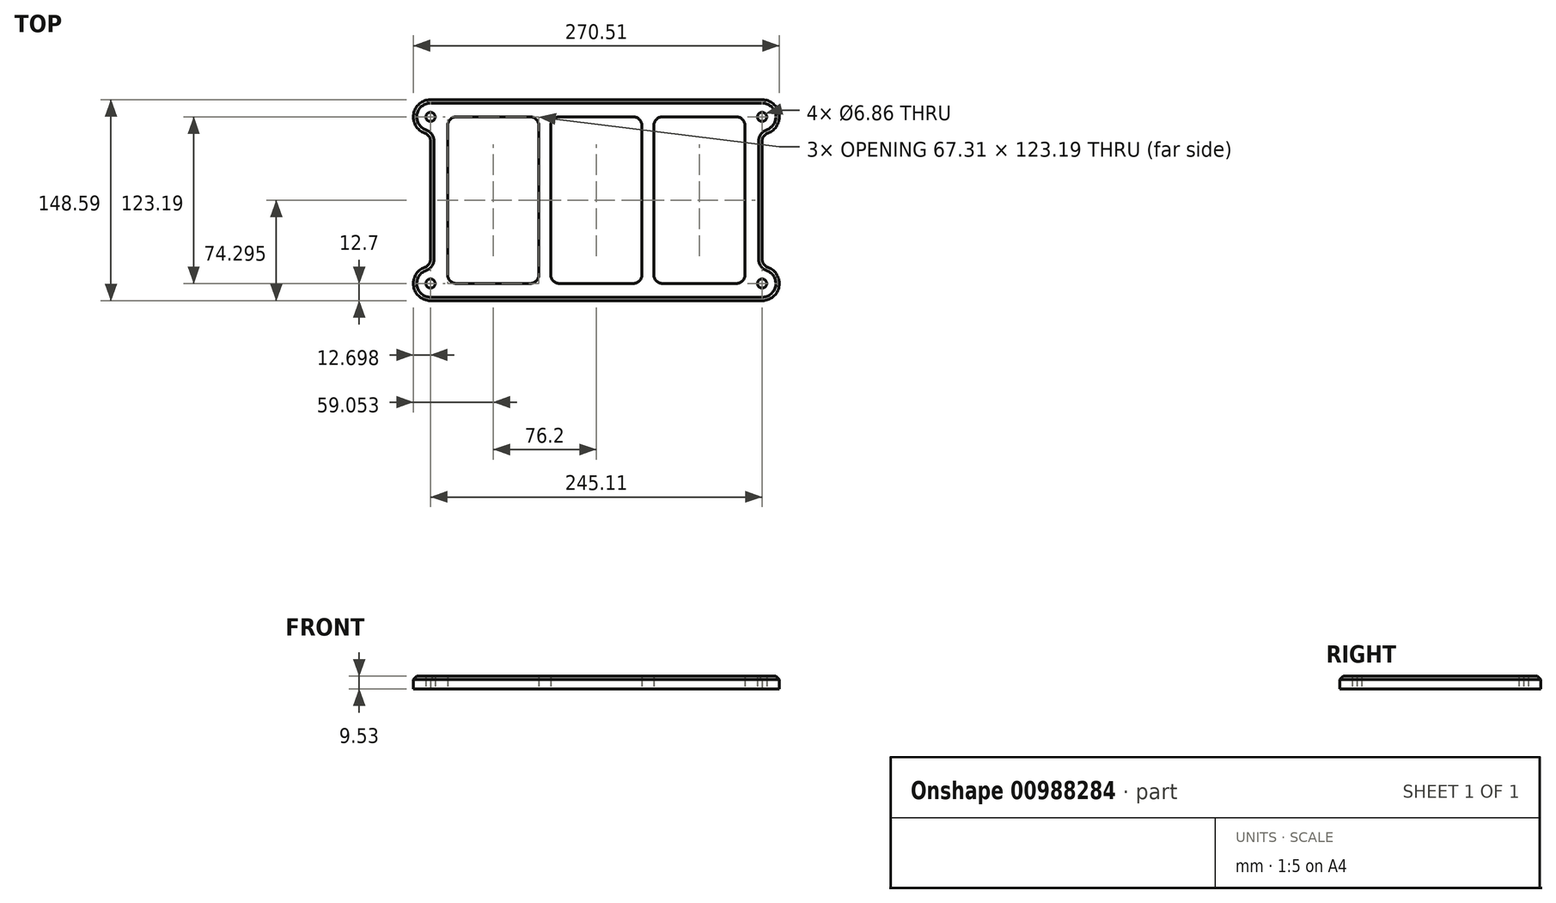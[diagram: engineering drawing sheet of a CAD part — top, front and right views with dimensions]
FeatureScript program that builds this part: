
annotation { "Feature Type Name" : "Feature", "Feature Type Description" : "" }
export const myFeature = defineFeature(function(context is Context, id is Id, definition is map)
    precondition{}
    {
        {
            var Q0;
            Q0=qCreatedBy(makeId("Top.planeOp"),FACE);
            var sketch = newSketch(context, id + "F0", { "sketchPlane" : qUnion([Q0])});
            skLineSegment(sketch, "E0.bottom", {"start": v(-240.31, 148.59) * mm, "end": v(-117.76, 148.59) * mm});
            skLineSegment(sketch, "E0.top", {"start": v(-240.31, 0) * mm, "end": v(-117.76, 0) * mm});
            skLineSegment(sketch, "E0.left", {"start": v(-240.31, 117.93) * mm, "end": v(-240.31, 30.66) * mm});
            skLineSegment(sketch, "E1.bottom", {"start": v(-221.26, 135.89) * mm, "end": v(-166.65, 135.89) * mm});
            skLineSegment(sketch, "E1.top", {"start": v(-221.26, 12.7) * mm, "end": v(-166.65, 12.7) * mm});
            skLineSegment(sketch, "E1.left", {"start": v(-227.61, 129.54) * mm, "end": v(-227.61, 19.05) * mm});
            skLineSegment(sketch, "E1.right", {"start": v(-160.3, 129.54) * mm, "end": v(-160.3, 19.05) * mm});
            skLineSegment(sketch, "E2.bottom", {"start": v(-145.06, 12.7) * mm, "end": v(-117.76, 12.7) * mm});
            skLineSegment(sketch, "E2.top", {"start": v(-145.06, 135.89) * mm, "end": v(-117.76, 135.9) * mm});
            skLineSegment(sketch, "E2.left", {"start": v(-151.41, 19.05) * mm, "end": v(-151.41, 129.54) * mm});
            skPoint(sketch, "E3.visualSharp", {"position": v(-232.42, 148.59) * mm});
            skPoint(sketch, "E4.visualSharp", {"position": v(-240.31, 9.53) * mm});
            skPoint(sketch, "E5.visualSharp", {"position": v(-231.78, 0) * mm});
            skPoint(sketch, "E6.visualSharp", {"position": v(-240.31, 135.89) * mm});
            skPoint(sketch, "E7.visualSharp", {"position": v(-151.41, 135.89) * mm});
            skArc(sketch, "E7.filletArc", {"start": v(-145.06, 135.89) * mm, "mid": v(-149.55, 134.03) * mm, "end": v(-151.41, 129.54) * mm});
            skPoint(sketch, "E8.visualSharp", {"position": v(-151.41, 12.7) * mm});
            skArc(sketch, "E8.filletArc", {"start": v(-151.41, 19.05) * mm, "mid": v(-149.55, 14.56) * mm, "end": v(-145.06, 12.7) * mm});
            skPoint(sketch, "E9.visualSharp", {"position": v(-160.3, 12.7) * mm});
            skArc(sketch, "E9.filletArc", {"start": v(-166.65, 12.7) * mm, "mid": v(-162.16, 14.56) * mm, "end": v(-160.3, 19.05) * mm});
            skPoint(sketch, "E10.visualSharp", {"position": v(-227.61, 12.7) * mm});
            skArc(sketch, "E10.filletArc", {"start": v(-227.61, 19.05) * mm, "mid": v(-225.75, 14.56) * mm, "end": v(-221.26, 12.7) * mm});
            skPoint(sketch, "E11.visualSharp", {"position": v(-227.61, 135.89) * mm});
            skArc(sketch, "E11.filletArc", {"start": v(-221.26, 135.89) * mm, "mid": v(-225.75, 134.03) * mm, "end": v(-227.61, 129.54) * mm});
            skPoint(sketch, "E12.visualSharp", {"position": v(-160.3, 135.89) * mm});
            skArc(sketch, "E12.filletArc", {"start": v(-160.3, 129.54) * mm, "mid": v(-162.16, 134.03) * mm, "end": v(-166.65, 135.89) * mm});
            skCircle(sketch, "E13", {"center": v(-240.31, 12.7) * mm, "radius": 3.43 * mm});
            skCircle(sketch, "E14", {"center": v(-240.31, 135.89) * mm, "radius": 3.43 * mm});
            skLineSegment(sketch, "E15", {"start": v(-193.96, 135.89) * mm, "end": v(-117.76, 135.9) * mm, "construction": true});
            skArc(sketch, "E16", {"start": v(-244.55, 24.67) * mm, "mid": v(-252.83, 10.55) * mm, "end": v(-240.31, 0) * mm});
            skPoint(sketch, "E17.visualSharp", {"position": v(-240.31, 25.4) * mm});
            skArc(sketch, "E17.filletArc", {"start": v(-244.55, 24.67) * mm, "mid": v(-241.48, 27) * mm, "end": v(-240.31, 30.66) * mm});
            skArc(sketch, "E18", {"start": v(-240.31, 148.59) * mm, "mid": v(-252.83, 138.04) * mm, "end": v(-244.55, 123.92) * mm});
            skPoint(sketch, "E19.visualSharp", {"position": v(-240.31, 123.19) * mm});
            skArc(sketch, "E19.filletArc", {"start": v(-240.31, 117.93) * mm, "mid": v(-241.48, 121.6) * mm, "end": v(-244.55, 123.92) * mm});
            skPoint(sketch, "E20.endSnap0", {"position": v(-117.76, 12.7) * mm});
            skLineSegment(sketch, "E21", {"start": v(-117.76, 0) * mm, "end": v(-117.76, 148.59) * mm});
            skArc(sketch, "E22.MirrorCS", {"start": v(9.03, 24.67) * mm, "mid": v(5.96, 27) * mm, "end": v(4.8, 30.66) * mm});
            skCircle(sketch, "E23.MirrorC", {"center": v(4.8, 135.89) * mm, "radius": 3.43 * mm});
            skArc(sketch, "E24.MirrorCS", {"start": v(4.8, 117.93) * mm, "mid": v(5.96, 121.6) * mm, "end": v(9.03, 123.92) * mm});
            skCircle(sketch, "E25.MirrorC", {"center": v(4.8, 12.7) * mm, "radius": 3.43 * mm});
            skArc(sketch, "E26.MirrorCS", {"start": v(-90.45, 135.9) * mm, "mid": v(-85.96, 134.03) * mm, "end": v(-84.1, 129.54) * mm});
            skArc(sketch, "E27.MirrorCS", {"start": v(-7.9, 19.05) * mm, "mid": v(-9.76, 14.56) * mm, "end": v(-14.25, 12.7) * mm});
            skArc(sketch, "E28.MirrorCS", {"start": v(-75.21, 129.54) * mm, "mid": v(-73.35, 134.03) * mm, "end": v(-68.86, 135.89) * mm});
            skArc(sketch, "E29.MirrorCS", {"start": v(-68.86, 12.7) * mm, "mid": v(-73.35, 14.56) * mm, "end": v(-75.21, 19.05) * mm});
            skArc(sketch, "E30.MirrorCS", {"start": v(-14.25, 135.89) * mm, "mid": v(-9.76, 134.03) * mm, "end": v(-7.9, 129.54) * mm});
            skArc(sketch, "E31.MirrorCS", {"start": v(-84.1, 19.05) * mm, "mid": v(-85.96, 14.56) * mm, "end": v(-90.45, 12.7) * mm});
            skPoint(sketch, "E32.MirrorP", {"position": v(4.8, 25.4) * mm});
            skLineSegment(sketch, "E33.MirrorCS", {"start": v(-90.45, 135.89) * mm, "end": v(-117.76, 135.9) * mm});
            skLineSegment(sketch, "E34.MirrorCS", {"start": v(-14.25, 135.89) * mm, "end": v(-68.86, 135.89) * mm});
            skLineSegment(sketch, "E35.MirrorCS", {"start": v(-7.9, 129.54) * mm, "end": v(-7.9, 19.05) * mm});
            skLineSegment(sketch, "E36.MirrorCS", {"start": v(4.8, 117.93) * mm, "end": v(4.8, 30.66) * mm});
            skLineSegment(sketch, "E37.MirrorCS", {"start": v(-84.1, 19.05) * mm, "end": v(-84.1, 129.54) * mm});
            skLineSegment(sketch, "E38.MirrorCS", {"start": v(4.8, 0) * mm, "end": v(-117.76, 0) * mm});
            skPoint(sketch, "E39.MirrorP", {"position": v(4.8, 123.19) * mm});
            skPoint(sketch, "E40.MirrorP", {"position": v(-84.1, 12.7) * mm});
            skArc(sketch, "E41.MirrorCS", {"start": v(9.03, 24.67) * mm, "mid": v(17.31, 10.55) * mm, "end": v(4.8, 0) * mm});
            skLineSegment(sketch, "E42.MirrorCS", {"start": v(-14.25, 12.7) * mm, "end": v(-68.86, 12.7) * mm});
            skPoint(sketch, "E43.MirrorP", {"position": v(4.8, 9.53) * mm});
            skLineSegment(sketch, "E44.MirrorCS", {"start": v(4.8, 148.59) * mm, "end": v(-117.76, 148.59) * mm});
            skPoint(sketch, "E45.MirrorP", {"position": v(-3.1, 148.59) * mm});
            skLineSegment(sketch, "E46.MirrorCS", {"start": v(-75.21, 129.54) * mm, "end": v(-75.21, 19.05) * mm});
            skLineSegment(sketch, "E47.MirrorCS", {"start": v(-41.56, 135.89) * mm, "end": v(-117.76, 135.89) * mm, "construction": true});
            skPoint(sketch, "E48.MirrorP", {"position": v(-84.1, 135.9) * mm});
            skArc(sketch, "E49.MirrorCS", {"start": v(4.8, 148.59) * mm, "mid": v(17.31, 138.04) * mm, "end": v(9.03, 123.92) * mm});
            skPoint(sketch, "E50.MirrorP", {"position": v(-3.74, 0) * mm});
            skPoint(sketch, "E51.MirrorP", {"position": v(-7.9, 12.7) * mm});
            skLineSegment(sketch, "E52.MirrorCS", {"start": v(-90.45, 12.7) * mm, "end": v(-117.76, 12.7) * mm});
            skPoint(sketch, "E53.MirrorP", {"position": v(-75.21, 135.89) * mm});
            skPoint(sketch, "E54.MirrorP", {"position": v(-7.9, 135.89) * mm});
            skPoint(sketch, "E55.MirrorP", {"position": v(-75.21, 12.7) * mm});
            skSolve(sketch);
        }
        {
            var Q0;
            Q0 = qSketchRegion(id + "F0", true);
            extrude(context, id + "F1", {"entities" : qUnion([Q0]), "depth" : 9.52 * mm, "offsetDistance" : 25.4 * mm});
        }
        {
            var Q0;
            Q0=makeQuery(id+"F1.opExtrude","CAP_EDGE",EDGE,{"disambiguationData":[OSD([sQuery(id+"F0.wireOp",EDGE,"E0.top")])],"isStart":false});
            chamfer(context, id + "F2", {"entities" : qUnion([Q0]), "width" : 2.54 * mm, "tangentPropagation" : true});
        }
    });
